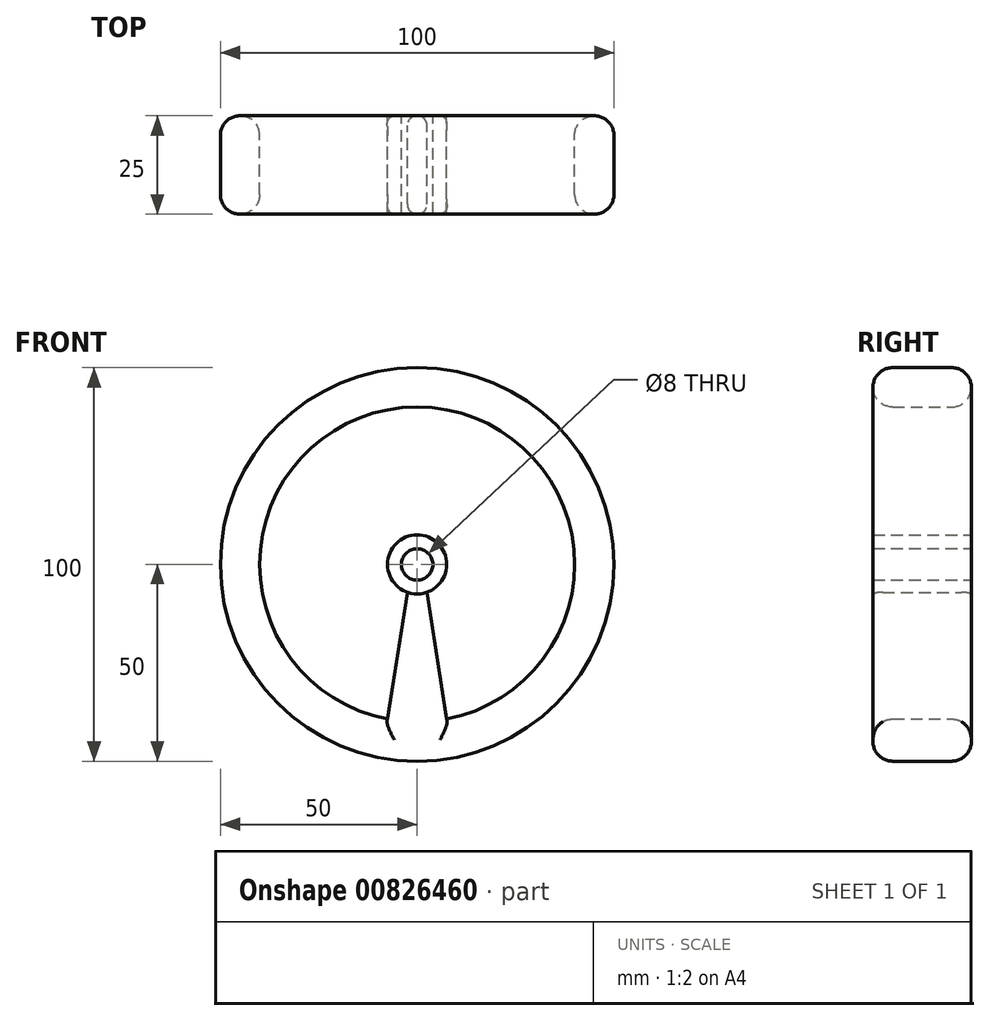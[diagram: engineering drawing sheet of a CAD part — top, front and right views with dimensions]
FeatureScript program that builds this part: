
annotation { "Feature Type Name" : "Feature", "Feature Type Description" : "" }
export const myFeature = defineFeature(function(context is Context, id is Id, definition is map)
    precondition{}
    {
        {
            var Q0;
            Q0=qCreatedBy(makeId("Front.planeOp"),FACE);
            var sketch = newSketch(context, id + "F0", { "sketchPlane" : qUnion([Q0])});
            skCircle(sketch, "E0", {"center": v(0, 0) * mm, "radius": 50 * mm});
            skCircle(sketch, "E1", {"center": v(0, 0) * mm, "radius": 4 * mm});
            skCircle(sketch, "E2", {"center": v(0, 0) * mm, "radius": 7.5 * mm});
            skCircle(sketch, "E3", {"center": v(0, 0) * mm, "radius": 40 * mm});
            skLineSegment(sketch, "E4", {"start": v(-2.5, -7.07) * mm, "end": v(-7.5, -39.3) * mm});
            skLineSegment(sketch, "E5", {"start": v(2.5, -7.07) * mm, "end": v(7.5, -39.3) * mm});
            skSolve(sketch);
        }
        {
            var Q0;
            {var subQ0=sQuery(id+"F0.wireOp",EDGE,"E4");Q0=makeQuery(id+"F0.imprint","IMPRINT",FACE,{"disambiguationData":[TD([[makeQuery(id+"F0.imprint","IMPRINT",EDGE,{"derivedFrom":subQ0}),1.0]])]});}
            var Q1;
            Q1=makeQuery(id+"F0.imprint","IMPRINT",FACE,{"disambiguationData":[TD([[makeQuery(id+"F0.imprint","IMPRINT",EDGE,{"derivedFrom":sQuery(id+"F0.wireOp",EDGE,"E0")}),1.0]])]});
            var Q2;
            Q2=makeQuery(id+"F0.imprint","IMPRINT",FACE,{"disambiguationData":[TD([[makeQuery(id+"F0.imprint","IMPRINT",EDGE,{"derivedFrom":sQuery(id+"F0.wireOp",EDGE,"E1")}),-1.0]])]});
            extrude(context, id + "F1", {"entities" : qUnion([Q0, Q1, Q2]), "endBound" : BoundingType.SYMMETRIC, "depth" : 25 * mm, "offsetDistance" : 25 * mm});
        }
        {
            var Q0;
            Q0=makeQuery(id+"F1.opExtrude","CAP_EDGE",EDGE,{"disambiguationData":[OSD([sQuery(id+"F0.wireOp",EDGE,"E5")])],"isStart":false});
            var Q1;
            Q1=makeQuery(id+"F1.opExtrude","CAP_EDGE",EDGE,{"disambiguationData":[OSD([sQuery(id+"F0.wireOp",EDGE,"E4")])],"isStart":false});
            var Q2;
            Q2=makeQuery(id+"F1.opExtrude","CAP_EDGE",EDGE,{"disambiguationData":[OSD([sQuery(id+"F0.wireOp",EDGE,"E4")])],"isStart":true});
            var Q3;
            Q3=makeQuery(id+"F1.opExtrude","CAP_EDGE",EDGE,{"disambiguationData":[OSD([sQuery(id+"F0.wireOp",EDGE,"E5")])],"isStart":true});
            fillet(context, id + "F2", {"entities" : qUnion([Q0, Q1, Q2, Q3]), "radius" : 2.5 * mm, "tangentPropagation" : true, "allowEdgeOverflow" : false});
        }
        {
            var Q0;
            Q0=makeQuery(id+"F1.opExtrude","CAP_EDGE",EDGE,{"disambiguationData":[OSD([sQuery(id+"F0.wireOp",EDGE,"E0")])],"isStart":false});
            var Q1;
            Q1=makeQuery(id+"F1.opExtrude","CAP_EDGE",EDGE,{"disambiguationData":[OSD([sQuery(id+"F0.wireOp",EDGE,"E0")])],"isStart":true});
            var Q2;
            Q2=makeQuery(id+"F1.opExtrude","CAP_EDGE",EDGE,{"disambiguationData":[OSD([sQuery(id+"F0.wireOp",EDGE,"E3")])],"isStart":true});
            var Q3;
            Q3=makeQuery(id+"F1.opExtrude","CAP_EDGE",EDGE,{"disambiguationData":[OSD([sQuery(id+"F0.wireOp",EDGE,"E3")])],"isStart":false});
            fillet(context, id + "F3", {"entities" : qUnion([Q0, Q1, Q2, Q3]), "radius" : 5 * mm, "tangentPropagation" : true, "allowEdgeOverflow" : false});
        }
    });
